# Revit family: ROLL OVER LIGHT 02_CM2W.2
name_source: partatom
category: Luminarias
units: mm (PartAtom-declared; Revit-internal decimal feet)

## family parameters
Compartido = No
Corte con vacíos al cargar = No
Cota de conector redondo = Diámetro de uso
Origen de luz = Sí
Punto de cálculo de habitación = No
Se basa en plano de trabajo = Sí
Siempre vertical = No
Tipo de pieza = Normal

## types (1)
- ROLL OVER LIGHT 02_CM2W.2
    Cambio de temperatura de color de luz atenuada = <Ninguno>
    Comentarios de vataje = 100-240V
    Descripción = LUMINARIA DE CORTESIA CIRCULAR EMPOTRABLE EN PISO, PRINCIPALMENTE EN ESTACIONAMIENTOS, CON UN PESO DE 2.3KG, CUERPO DE ALUMINIO FUNDIDO A PRESION CUBIERTO CON POLVO GRIS, USO PARA INTERIORES O EXTERIORES IP67, ALTA RESISTENCIA AL IMPACTO IK10, 6 LEDS DE 0.5W TIPO SMD3030 CON UNA POTENCIA TOTAL DE 3.9W, 150 LUMENES, EFICIENCIA DE 38.46LM/W, TEMPERATURA DE BLANCO CALIDO 3000K, CORRIENTE DE OPERACIÓN EN 57mA, DIMMEABLE OPCIONAL POR TRIAC, HOUSING DE PVC 157mm EN DIAMENTRO y 150mm DE PROFUNDIDAD, CABLE DE 0.5M H05RN-F, ALIMENTADA A 100-240V.
    Elevación por defecto = 0 mm  [stored 0 ft]
    Fabricante = BRILLANT
    Filtro de color = 16777215
    Lámpara = SMD 3030
    Modelo = CM2W.2
    Tamaño de símbolo de origen de luz = 610 mm
    Watt per fixture = 3

note: [stored X ft] marks values corroborated as IEEE doubles in the binary element streams (Revit-internal decimal feet)

## geometry (parser evidence)
native form markers: Blend x2
no freeform markers — native parametric forms only
